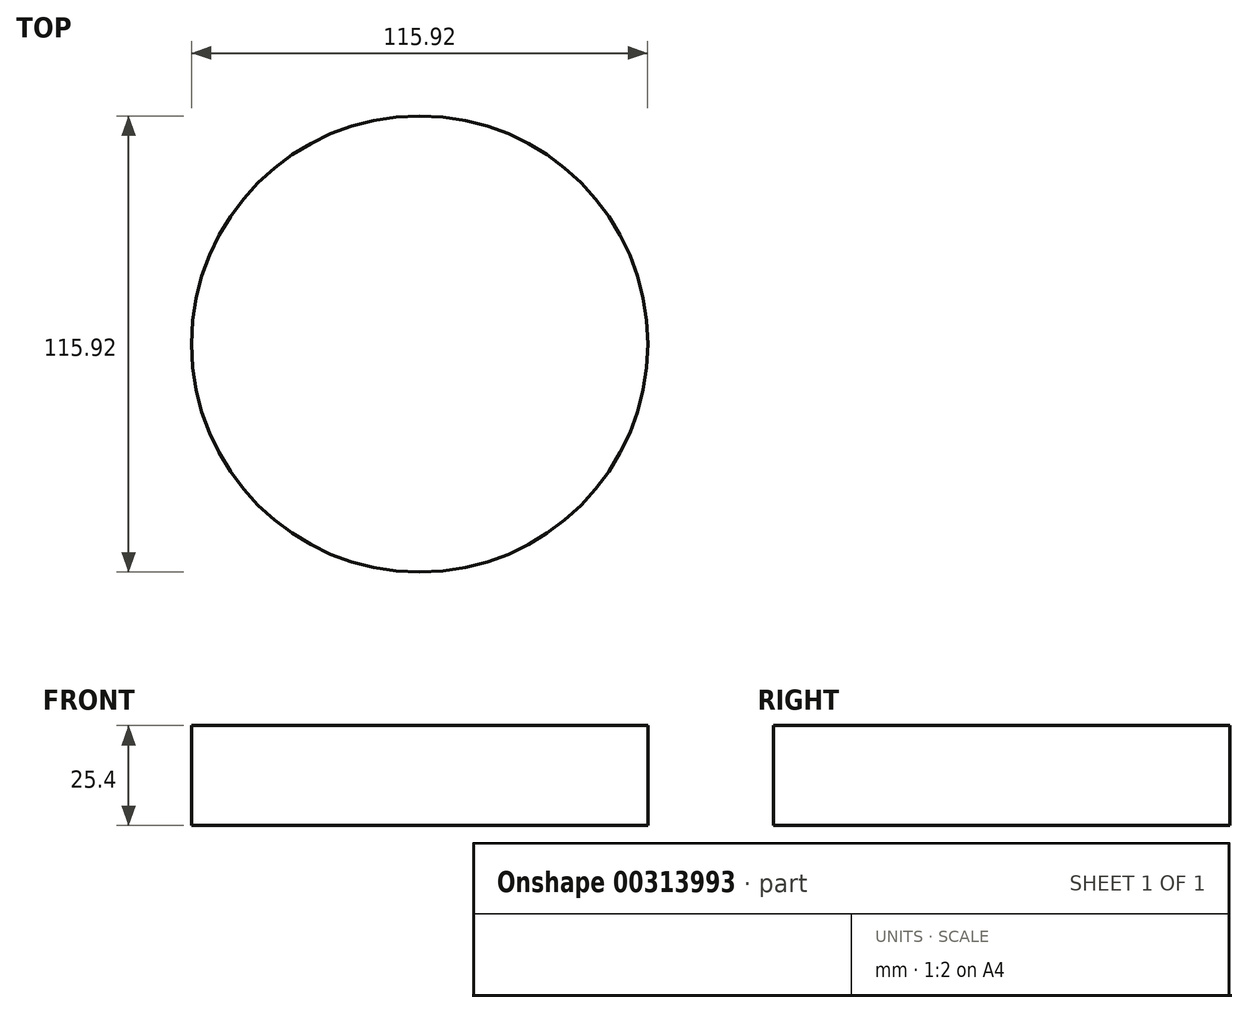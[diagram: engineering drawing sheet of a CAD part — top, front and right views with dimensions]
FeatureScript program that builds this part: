
annotation { "Feature Type Name" : "Feature", "Feature Type Description" : "" }
export const myFeature = defineFeature(function(context is Context, id is Id, definition is map)
    precondition{}
    {
        {
            var Q0;
            Q0=qCreatedBy(makeId("Top.planeOp"),FACE);
            var sketch = newSketch(context, id + "F0", { "sketchPlane" : qUnion([Q0])});
            skCircle(sketch, "E0", {"center": v(0, 0) * mm, "radius": 57.96 * mm});
            skSolve(sketch);
        }
        {
            var Q0;
            Q0 = qSketchRegion(id + "F0", true);
            extrude(context, id + "F1", {"entities" : qUnion([Q0]), "depth" : 25.4 * mm});
        }
        {
            var Q0;
            Q0=qCreatedBy(makeId("Top.planeOp"),FACE);
            var sketch = newSketch(context, id + "F2", { "sketchPlane" : qUnion([Q0])});
            skCircle(sketch, "E1.0", {"center": v(0, 0) * mm, "radius": 57.96 * mm});
            skCircle(sketch, "E2", {"center": v(0, 0) * mm, "radius": 32.98 * mm});
            skSolve(sketch);
        }
        {
            var Q0;
            Q0=makeQuery(id+"F2.imprint","IMPRINT",FACE,{"disambiguationData":[TD([[makeQuery(id+"F2.imprint","IMPRINT",EDGE,{"derivedFrom":sQuery(id+"F2.wireOp",EDGE,"E2")}),1.0]])]});
            var Q1;
            Q1=makeQuery(id+"F1.opExtrude","CAP_FACE",FACE,{"disambiguationData":[OSD([sQuery(id+"F0.wireOp",EDGE,"E0")])],"isStart":true});
            extrude(context, id + "F3", {"entities" : qUnion([Q0, Q1]), "operationType" : NewBodyOperationType.ADD, "depth" : 25.4 * mm});
        }
        {
            var Q0;
            Q0=qCreatedBy(makeId("Top.planeOp"),FACE);
            var sketch = newSketch(context, id + "F4", { "sketchPlane" : qUnion([Q0])});
            skCircle(sketch, "E3.0", {"center": v(0, 0) * mm, "radius": 57.96 * mm});
            skCircle(sketch, "E4", {"center": v(0, 0) * mm, "radius": 563.27 * mm, "construction": true});
            skSolve(sketch);
        }
        {
            var Q0;
            Q0 = qSketchRegion(id + "F4", true);
            extrude(context, id + "F5", {"entities" : qUnion([Q0]), "operationType" : NewBodyOperationType.ADD, "depth" : 25.4 * mm});
        }
    });
